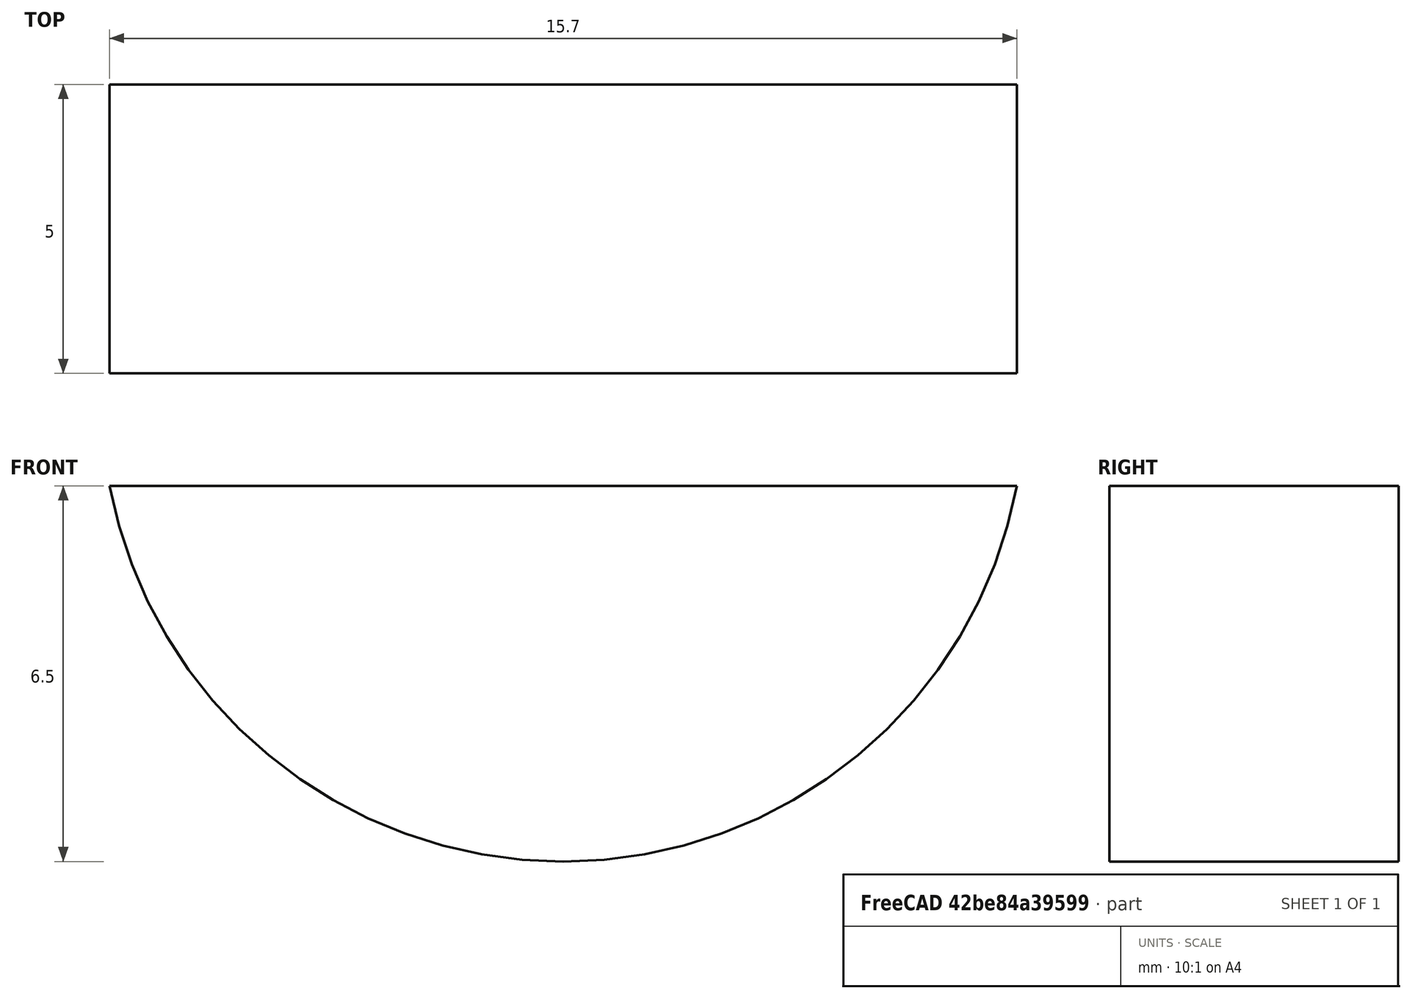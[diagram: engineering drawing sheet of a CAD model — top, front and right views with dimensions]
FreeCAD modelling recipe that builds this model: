
FCSTD DOCUMENT  (FreeCAD 0.20R29126 (Git))
Label: electric-motor-woodruff-key
License: All rights reserved
LicenseURL: http://en.wikipedia.org/wiki/All_rights_reserved
objects: Sketcher::SketchObject×1, PartDesign::Pad×1, PartDesign::Body×1
note: 4 computed .brp shape members not serialized (recipe doc carries the construction recipe); baked Part::Feature solids carry a one-line shape summary decoded from their .brp

FEATURE [Sketcher::SketchObject] Sketch
  FullyConstrained = true
  MapMode = 5
  Placement = pos=(0,0,0) rot=(1,0,0;1.5708rad)
  Support = -> [XZ_Plane]
  sketch-geometry (3):
    g0: ArcOfCircle CenterX=0 CenterY=1.49019 CenterZ=0 NormalX=0 NormalY=0 NormalZ=1 AngleXU=0 Radius=7.99019 StartAngle=3.32919 EndAngle=6.09558
    g1: LineSegment StartX=-7.85 StartY=2.4e-15 StartZ=0 EndX=7.85 EndY=2.4e-15 EndZ=0
    g2: LineSegment StartX=0 StartY=0 StartZ=0 EndX=0 EndY=-6.5 EndZ=0
  constraints (10):
    c: PointOnObject(g0,g-2)
    c: Horizontal(g1)
    c: Coincident(g0,g1)
    c: Coincident(g0,g1)
    c: PointOnObject(g2,g1)
    c: PointOnObject(g2,g0)
    c: Vertical(g2)
    c: DistanceX(g1,g1) = 15.7
    c: DistanceY(g2,g0) = 6.5
    c: Coincident(g2,g-1)
FEATURE [PartDesign::Pad] Pad
  Direction = (0,-1,2e-16)
  Length = 5
  Length2 = 10
  Midplane = true
  Placement = pos=(0,0,0) rot=(1,0,0;1.5708rad)
  Profile = -> Sketch
  ReferenceAxis = -> Sketch [N_Axis]
  Type = 0
FEATURE [PartDesign::Body] Body
  Group = -> [Sketch,Pad]
  Origin = -> Origin
  Tip = -> Pad
